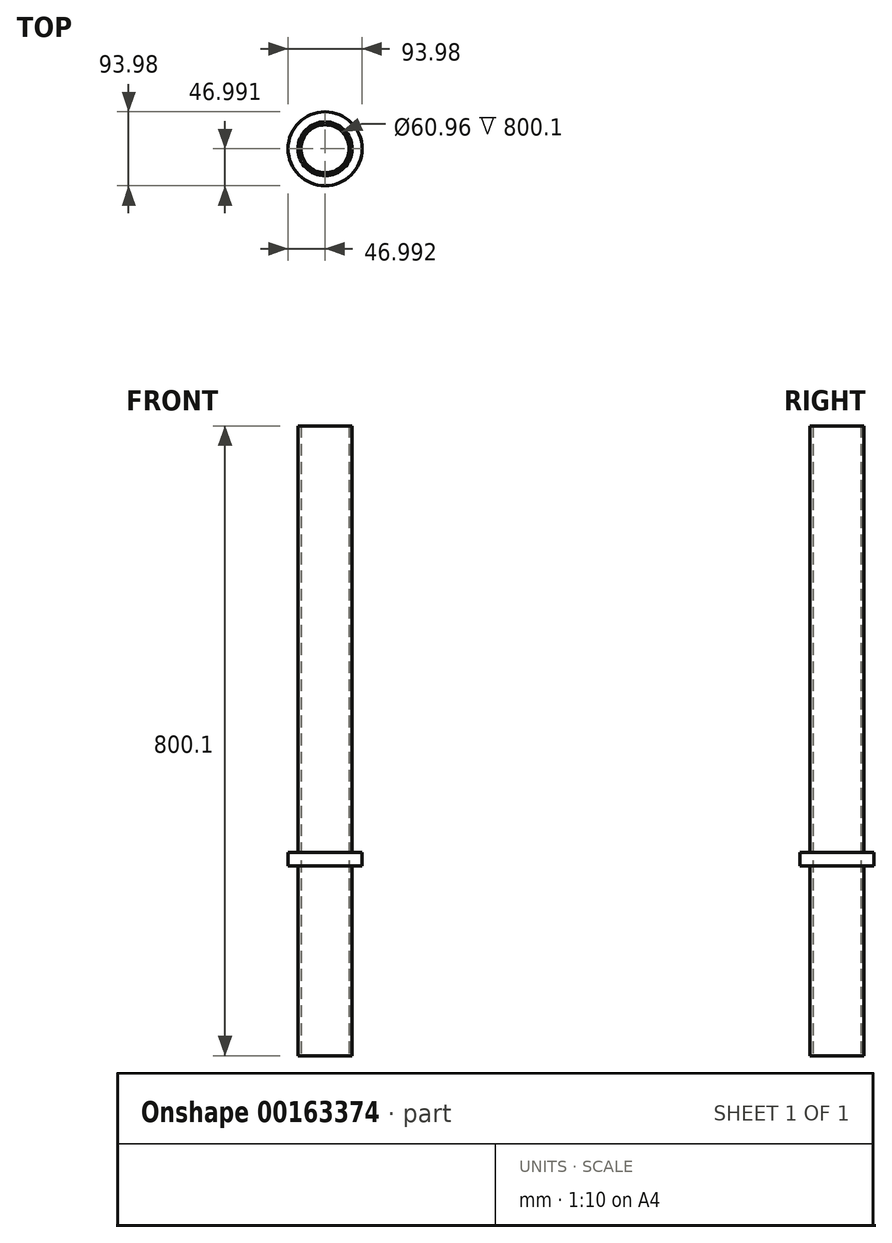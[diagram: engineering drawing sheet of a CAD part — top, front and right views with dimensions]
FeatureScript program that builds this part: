
annotation { "Feature Type Name" : "Feature", "Feature Type Description" : "" }
export const myFeature = defineFeature(function(context is Context, id is Id, definition is map)
    precondition{}
    {
        {
            var Q0;
            Q0=qCreatedBy(makeId("Top.planeOp"),FACE);
            var sketch = newSketch(context, id + "F0", { "sketchPlane" : qUnion([Q0])});
            skCircle(sketch, "E0", {"center": v(-27.87, 21.56) * mm, "radius": 34.3 * mm});
            skSolve(sketch);
        }
        {
            var Q0;
            Q0=makeQuery(id+"F0.imprint","IMPRINT",FACE,{"disambiguationData":[TD([[makeQuery(id+"F0.imprint","IMPRINT",EDGE,{"derivedFrom":sQuery(id+"F0.wireOp",EDGE,"E0")}),1.0]])]});
            extrude(context, id + "F1", {"entities" : qUnion([Q0]), "depth" : 558.8 * mm});
        }
        {
            var Q0;
            Q0=makeQuery(id+"F1.opExtrude","CAP_FACE",FACE,{"disambiguationData":[OSD([sQuery(id+"F0.wireOp",EDGE,"E0")])],"isStart":true});
            var sketch = newSketch(context, id + "F2", { "sketchPlane" : qUnion([Q0])});
            skCircle(sketch, "E1", {"center": v(-27.87, -21.56) * mm, "radius": 47 * mm});
            skSolve(sketch);
        }
        {
            var Q0;
            Q0=makeQuery(id+"F2.imprint","IMPRINT",FACE,{"disambiguationData":[TD([[makeQuery(id+"F2.imprint","IMPRINT",EDGE,{"derivedFrom":sQuery(id+"F2.wireOp",EDGE,"E1")}),1.0]])]});
            extrude(context, id + "F3", {"entities" : qUnion([Q0]), "operationType" : NewBodyOperationType.ADD, "oppositeDirection" : true, "depth" : 16.76 * mm});
        }
        {
            var Q0;
            {var subQ0=sQuery(id+"F0.wireOp",EDGE,"E0");Q0=makeQuery(id+"F3.boolean.opBoolean","MERGE",FACE,{"derivedFrom":[makeQuery(id+"F1.opExtrude","CAP_FACE",FACE,{"disambiguationData":[OSD([subQ0])],"isStart":true}),makeQuery(id+"F3.opExtrude","CAP_FACE",FACE,{"disambiguationData":[OSD([subQ0,sQuery(id+"F2.wireOp",EDGE,"E1")])],"isStart":true})]});}
            var sketch = newSketch(context, id + "F4", { "sketchPlane" : qUnion([Q0])});
            skCircle(sketch, "E2", {"center": v(-27.87, -21.56) * mm, "radius": 34.3 * mm});
            skSolve(sketch);
        }
        {
            var Q0;
            Q0=makeQuery(id+"F4.imprint","IMPRINT",FACE,{"disambiguationData":[TD([[makeQuery(id+"F4.imprint","IMPRINT",EDGE,{"derivedFrom":sQuery(id+"F4.wireOp",EDGE,"E2")}),1.0]])]});
            extrude(context, id + "F5", {"entities" : qUnion([Q0]), "operationType" : NewBodyOperationType.ADD, "depth" : 241.3 * mm});
        }
        {
            var Q0;
            Q0=makeQuery(id+"F5.opExtrude","CAP_FACE",FACE,{"disambiguationData":[OSD([sQuery(id+"F4.wireOp",EDGE,"E2")])],"isStart":false});
            var sketch = newSketch(context, id + "F6", { "sketchPlane" : qUnion([Q0])});
            skLineSegment(sketch, "E3.bottom", {"start": v(5.78, -14.94) * mm, "end": v(-61.86, -14.94) * mm});
            skLineSegment(sketch, "E3.top", {"start": v(5.78, -26.07) * mm, "end": v(-61.86, -26.07) * mm});
            skLineSegment(sketch, "E3.left", {"start": v(5.78, -14.94) * mm, "end": v(5.78, -26.07) * mm});
            skLineSegment(sketch, "E3.right", {"start": v(-61.86, -14.94) * mm, "end": v(-61.86, -26.07) * mm});
            skSolve(sketch);
        }
        {
            var Q0;
            {var subQ1=sQuery(id+"F6.wireOp",EDGE,"E3.top");Q0=makeQuery(id+"F6.imprint","IMPRINT",FACE,{"disambiguationData":[TD([[makeQuery(id+"F6.imprint","IMPRINT",EDGE,{"derivedFrom":subQ1}),-1.0]])]});}
            extrude(context, id + "F7", {"entities" : qUnion([Q0]), "operationType" : NewBodyOperationType.ADD, "oppositeDirection" : true, "depth" : 38.35 * mm});
        }
        {
            var Q0;
            Q0=makeQuery(id+"F5.opExtrude","CAP_FACE",FACE,{"disambiguationData":[OSD([sQuery(id+"F4.wireOp",EDGE,"E2")])],"isStart":false});
            var sketch = newSketch(context, id + "F8", { "sketchPlane" : qUnion([Q0])});
            skCircle(sketch, "E4", {"center": v(-27.87, -21.56) * mm, "radius": 17.8 * mm});
            skSolve(sketch);
        }
        {
            var Q0;
            Q0=sQuery(id+"F8.wireOp",VERTEX,"E4.center");
            var Q1;
            Q1=makeQuery(id+"F1.opExtrude","SWEPT_BODY",BODY,{"disambiguationData":[OSD([sQuery(id+"F0.wireOp",EDGE,"E0")])]});
            hole(context, id + "F9", {"style" : HoleStyle.SIMPLE, "endStyle" : HoleEndStyle.THROUGH, "holeDiameter" : 60.96 * mm, "locations" : qUnion([Q0]), "scope" : qUnion([Q1]), "isTappedThrough" : true});
        }
    });
